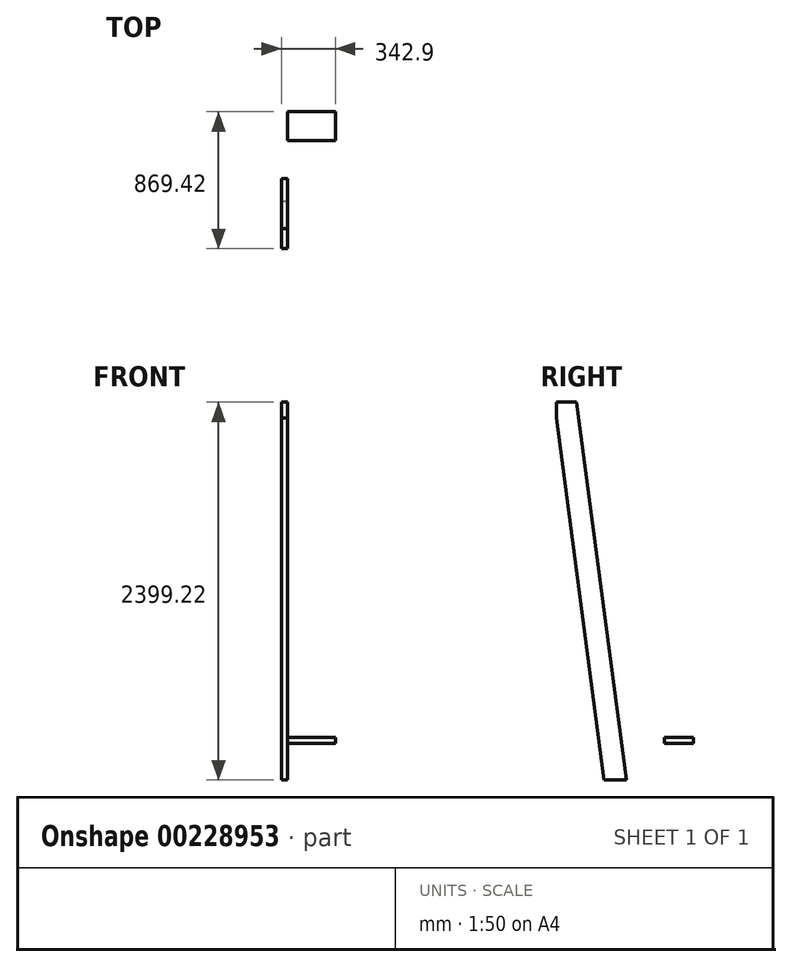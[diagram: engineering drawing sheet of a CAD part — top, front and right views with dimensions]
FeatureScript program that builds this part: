
annotation { "Feature Type Name" : "Feature", "Feature Type Description" : "" }
export const myFeature = defineFeature(function(context is Context, id is Id, definition is map)
    precondition{}
    {
        {
            var Q0;
            Q0=qCreatedBy(makeId("Right.planeOp"),FACE);
            cPlane(context, id + "F0", {"entities" : qUnion([Q0]), "cplaneType" : CPlaneType.OFFSET, "offset" : 609.6 * mm, "width" : 152.4 * mm, "height" : 152.4 * mm});
        }
        {
            var Q0;
            Q0=qCreatedBy(makeId("Right.planeOp"),FACE);
            var sketch = newSketch(context, id + "F1", { "sketchPlane" : qUnion([Q0])});
            skLineSegment(sketch, "E0.bottom", {"start": v(-177.79, 2417.48) * mm, "end": v(-316.3, 2399.22) * mm, "construction": true});
            skLineSegment(sketch, "E0.top", {"start": v(140.9, 0) * mm, "end": v(2.4, -18.26) * mm, "construction": true});
            skLineSegment(sketch, "E0.left", {"start": v(-177.79, 2417.48) * mm, "end": v(-175.38, 2399.22) * mm, "construction": true});
            skLineSegment(sketch, "E0.right", {"start": v(-316.3, 2399.22) * mm, "end": v(0, 0) * mm});
            skLineSegment(sketch, "E1", {"start": v(0, 0) * mm, "end": v(140.9, 0) * mm});
            skLineSegment(sketch, "E2", {"start": v(-316.3, 2399.22) * mm, "end": v(-175.38, 2399.22) * mm});
            skLineSegment(sketch, "E3", {"start": v(-175.38, 2399.22) * mm, "end": v(140.9, 0) * mm});
            skLineSegment(sketch, "E4", {"start": v(0, 0) * mm, "end": v(2.4, -18.26) * mm, "construction": true});
            skSolve(sketch);
        }
        {
            var Q0;
            Q0=makeQuery(id+"F1.imprint","IMPRINT",FACE,{"disambiguationData":[TD([[makeQuery(id+"F1.imprint","IMPRINT",EDGE,{"derivedFrom":sQuery(id+"F1.wireOp",EDGE,"E0.right")}),1.0]])]});
            extrude(context, id + "F2", {"entities" : qUnion([Q0]), "oppositeDirection" : true, "depth" : 38.1 * mm});
        }
        {
            var Q0;
            Q0=qCreatedBy(makeId("Right.planeOp"),FACE);
            var sketch = newSketch(context, id + "F3", { "sketchPlane" : qUnion([Q0])});
            skLineSegment(sketch, "E5.bottom", {"start": v(382.37, 270.38) * mm, "end": v(566.52, 270.38) * mm});
            skLineSegment(sketch, "E5.top", {"start": v(382.37, 232.28) * mm, "end": v(566.52, 232.28) * mm});
            skLineSegment(sketch, "E5.left", {"start": v(382.37, 270.38) * mm, "end": v(382.37, 232.28) * mm});
            skLineSegment(sketch, "E5.right", {"start": v(566.52, 270.38) * mm, "end": v(566.52, 232.28) * mm});
            skSolve(sketch);
        }
        {
            var Q0;
            Q0=makeQuery(id+"F3.imprint","IMPRINT",FACE,{"disambiguationData":[TD([[makeQuery(id+"F3.imprint","IMPRINT",EDGE,{"derivedFrom":sQuery(id+"F3.wireOp",EDGE,"E5.bottom")}),-1.0]])]});
            extrude(context, id + "F4", {"entities" : qUnion([Q0]), "depth" : 304.8 * mm});
        }
        {
            var Q0;
            Q0=makeQuery(id+"F1.imprint","IMPRINT",FACE,{"disambiguationData":[TD([[makeQuery(id+"F1.imprint","IMPRINT",EDGE,{"derivedFrom":sQuery(id+"F1.wireOp",EDGE,"E0.right")}),1.0]])]});
            var sketch = newSketch(context, id + "F5", { "sketchPlane" : qUnion([Q0])});
            skLineSegment(sketch, "E6.0", {"start": v(-316.3, 2399.22) * mm, "end": v(0, 0) * mm, "construction": true});
            skPoint(sketch, "E7", {"position": v(-35.16, 266.7) * mm});
            skSolve(sketch);
        }
        {
            var Q0;
            Q0=makeQuery(id+"F2.opExtrude","CAP_FACE",FACE,{"disambiguationData":[OSD([sQuery(id+"F1.wireOp",EDGE,"E0.right"),sQuery(id+"F1.wireOp",EDGE,"E1"),sQuery(id+"F1.wireOp",EDGE,"E2"),sQuery(id+"F1.wireOp",EDGE,"E3")])],"isStart":false});
            var sketch = newSketch(context, id + "F6", { "sketchPlane" : qUnion([Q0])});
            skLineSegment(sketch, "E8.0", {"start": v(316.3, 2399.22) * mm, "end": v(0, 0) * mm});
            skPoint(sketch, "E9", {"position": v(70.32, 533.4) * mm});
            skSolve(sketch);
        }
        {
            var Q0;
            Q0=makeQuery(id+"F1.imprint","IMPRINT",FACE,{"disambiguationData":[TD([[makeQuery(id+"F1.imprint","IMPRINT",EDGE,{"derivedFrom":sQuery(id+"F1.wireOp",EDGE,"E0.right")}),1.0]])]});
            var sketch = newSketch(context, id + "F7", { "sketchPlane" : qUnion([Q0])});
            skLineSegment(sketch, "E10.0", {"start": v(-316.3, 2399.22) * mm, "end": v(-175.38, 2399.22) * mm});
            skLineSegment(sketch, "E11.0", {"start": v(-316.3, 2399.22) * mm, "end": v(0, 0) * mm});
            skLineSegment(sketch, "E12", {"start": v(-302.9, 2399.22) * mm, "end": v(-302.9, 2297.62) * mm});
            skSolve(sketch);
        }
        {
            var Q0;
            Q0=qSketchRegion(id+"F7",true);
            extrude(context, id + "F8", {"entities" : qUnion([Q0]), "operationType" : NewBodyOperationType.REMOVE, "endBound" : BoundingType.THROUGH_ALL, "oppositeDirection" : true, "depth" : 25.4 * mm});
        }
    });
